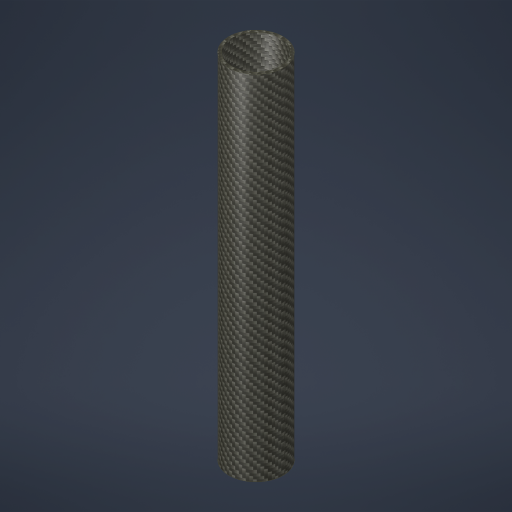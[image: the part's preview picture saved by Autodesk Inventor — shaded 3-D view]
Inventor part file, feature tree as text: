
AUTODESK INVENTOR PART (.ipt)
format: ipt  version: 2023.4 (Build 274418000, 418)  size: 236,544 bytes
history: native  units: in
note: dims shown in document units (in); Inventor stores cm internally (conversion verified against a paired STEP export)
features: extrude x1, sketch x1
ambient origin geometry x8: Origin, YZ Plane, XZ Plane, XY Plane, X Axis, Y Axis, Z Axis, Center Point
bodies: Solid1 (feature_tree)
feature tree (2):
  extrude  "Extrusion1"  Depth=13.0in
  sketch  "Sketch1"  dims[d0=2.0in d1=0.1in d2=13.0in d3=0.0in]
